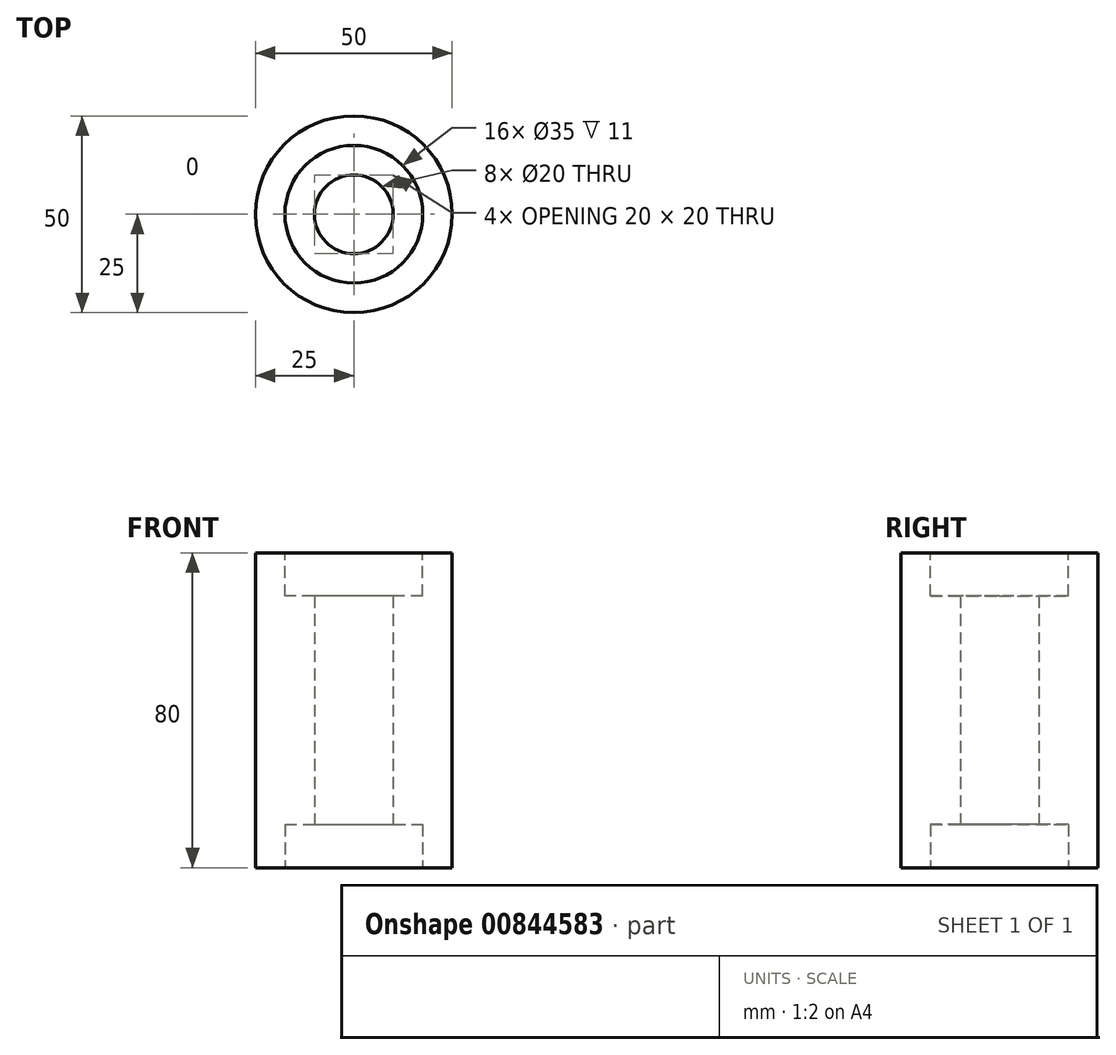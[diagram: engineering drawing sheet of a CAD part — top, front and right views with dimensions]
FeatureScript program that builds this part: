
annotation { "Feature Type Name" : "Feature", "Feature Type Description" : "" }
export const myFeature = defineFeature(function(context is Context, id is Id, definition is map)
    precondition{}
    {
        {
            var Q0;
            Q0=qCreatedBy(makeId("Top.planeOp"),FACE);
            var sketch = newSketch(context, id + "F0", { "sketchPlane" : qUnion([Q0])});
            skCircle(sketch, "E0", {"center": v(0, 0) * mm, "radius": 25 * mm});
            skSolve(sketch);
        }
        {
            var Q0;
            Q0=makeQuery(id+"F0.imprint","IMPRINT",FACE,{"disambiguationData":[TD([[makeQuery(id+"F0.imprint","IMPRINT",EDGE,{"derivedFrom":sQuery(id+"F0.wireOp",EDGE,"E0")}),1.0]])]});
            extrude(context, id + "F1", {"entities" : qUnion([Q0]), "depth" : 80 * mm, "offsetDistance" : 25 * mm});
        }
        {
            var Q0;
            Q0=makeQuery(id+"F1.opExtrude","CAP_FACE",FACE,{"disambiguationData":[OSD([sQuery(id+"F0.wireOp",EDGE,"E0")])],"isStart":false});
            var sketch = newSketch(context, id + "F2", { "sketchPlane" : qUnion([Q0])});
            skCircle(sketch, "E1", {"center": v(0, 0) * mm, "radius": 17.5 * mm});
            skSolve(sketch);
        }
        {
            var Q0;
            Q0=makeQuery(id+"F2.imprint","IMPRINT",FACE,{"disambiguationData":[TD([[makeQuery(id+"F2.imprint","IMPRINT",EDGE,{"derivedFrom":sQuery(id+"F2.wireOp",EDGE,"E1")}),1.0]])]});
            extrude(context, id + "F3", {"entities" : qUnion([Q0]), "operationType" : NewBodyOperationType.REMOVE, "oppositeDirection" : true, "depth" : 11 * mm, "offsetDistance" : 25 * mm});
        }
        {
            var Q0;
            Q0=makeQuery(id+"F1.opExtrude","CAP_FACE",FACE,{"disambiguationData":[OSD([sQuery(id+"F0.wireOp",EDGE,"E0")])],"isStart":true});
            var sketch = newSketch(context, id + "F4", { "sketchPlane" : qUnion([Q0])});
            skCircle(sketch, "E2", {"center": v(0, 0) * mm, "radius": 17.5 * mm});
            skSolve(sketch);
        }
        {
            var Q0;
            Q0=makeQuery(id+"F4.imprint","IMPRINT",FACE,{"disambiguationData":[TD([[makeQuery(id+"F4.imprint","IMPRINT",EDGE,{"derivedFrom":sQuery(id+"F4.wireOp",EDGE,"E2")}),1.0]])]});
            extrude(context, id + "F5", {"entities" : qUnion([Q0]), "operationType" : NewBodyOperationType.REMOVE, "oppositeDirection" : true, "depth" : 11 * mm, "offsetDistance" : 25 * mm});
        }
        {
            var Q0;
            Q0=makeQuery(id+"F5.boolean.opBoolean","COPY",FACE,{"derivedFrom":makeQuery(id+"F5.opExtrude","CAP_FACE",FACE,{"disambiguationData":[OSD([sQuery(id+"F4.wireOp",EDGE,"E2")])],"isStart":false})});
            var sketch = newSketch(context, id + "F6", { "sketchPlane" : qUnion([Q0])});
            skCircle(sketch, "E3", {"center": v(0, 0) * mm, "radius": 10 * mm});
            skSolve(sketch);
        }
        {
            var Q0;
            Q0 = qSketchRegion(id + "F6", true);
            extrude(context, id + "F7", {"entities" : qUnion([Q0]), "operationType" : NewBodyOperationType.REMOVE, "oppositeDirection" : true, "depth" : 100 * mm, "offsetDistance" : 25 * mm});
        }
    });
